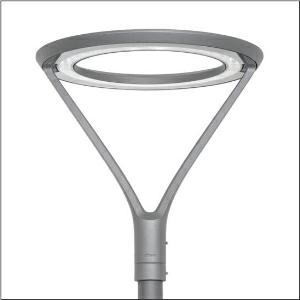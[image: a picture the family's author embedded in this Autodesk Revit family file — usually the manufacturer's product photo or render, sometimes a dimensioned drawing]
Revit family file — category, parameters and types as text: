
# Revit family: dl_r__20___st1_2a_5xa512832a008p_5178
name_source: partatom
category: Lighting Fixtures
units: mm (PartAtom-declared; Revit-internal decimal feet)

## family parameters
Cut with Voids When Loaded = No
Host = Face
Light Source = No
Part Type = Normal
Room Calculation Point = No
Round Connector Dimension = Use Diameter
Shared = No

## types (1)
- --- (1 x LED, 4200 lm, 43.6 W, 2200K)
    Apparent Load = 44 VA
    CIE Flux Codes = 32 72 97 100 100
    Color Rendering = 70
    Color Temperature = 2200K
    Default Elevation = 1800 mm
    Description = DL® 20, mast luminaire, primary light control with reflector, highly specular, primary optical cover: cover, of toughened safety glass of clear glass with excellent transmission level, light distribution: ST1.2a, light emission: direct distribution, primary light characteristic: asymmetric, installation type: post-top, LED, High Power LED, rated luminous flux: 4.180lm, luminous efficacy: 79lm/W, light colour: 722, colour temperature: 2200K, control gear: ECG Plus, control: flexible luminous flux parameterisation, time-dependent luminous flux control, constant luminous flux control, digital communication interface, power reduction, overheat protection, electronic power reduction, mains connection: 230..240V, 50/60Hz, connection cable pre-assembled, cable length: 5m, start of lifetime: 53W, end of service life: 54W, reduction: 24W, luminaire housing, upper part, of cast aluminium, powder-coated, Siteco® metallic grey (DB 702S), diameter: 690mm, height: 690mm, spigot size: 76mm (post-top), luminaire housing, of cast aluminium, powder-coated, Siteco® metallic grey (DB 702S), equipment: Power, protection rating (complete): IP66, insulation class (complete): insulation class II (safety insulation), certification: CE, ENEC, VDE, impact resistance: IK08, permissible operating ambient temperature: -25..+30°C, standard-compliant lighting for roads and squares, packaging unit: 1 piece

Light Distribution: ST1.2a
    Height = 690 mm
    Lamp = 1 x LED
    Lamp Light Flux = 4200 lm
    Lamp Power = 43.6 W
    Lamp count = 1
    Length = 690 mm
    Luminous efficacy = 96 lm/W
    Manufacturer = Siteco
    ModVariant = No
    Model = 5XA512832A008P
    Number of Poles = 1
    OnlyDefault = Yes
    Power Factor = 1
    Product Name = DL® 20 | ST1.2a
    Product group = mast luminaire | pylon top
    ProductGroupID = 6100
    Protection Class = Protection class II
    Protection Degree = IP 66
    RLX_Detail_Level = 1
    RLX_Emergency_Light_Flux = 0 lm
    RLX_Emergency_Type = 0
    RLX_Emergency_Type_DB = No
    RlxData = <blob elided: 206837 chars, md5=46a01574>
    Socket = socket
    Standby Power = 0 W
    System Light Flux = 4200 lm
    System Power = 44 W
    Type Comments = factory setting: luminous flux: 100 % | dim-lin: 254 | 587 mA
    Type Image = l_1006001.jpg
    URL = http://relux.com
    VarID = @adj_028427
    Voltage = 0 V
    Weight = 0.00 kg
    Width = 0 mm  [stored 0 ft]

note: [stored X ft] marks values corroborated as IEEE doubles in the binary element streams (Revit-internal decimal feet)

## geometry (parser evidence)
native form markers: Blend x4, Sweep x12
no freeform markers — native parametric forms only
